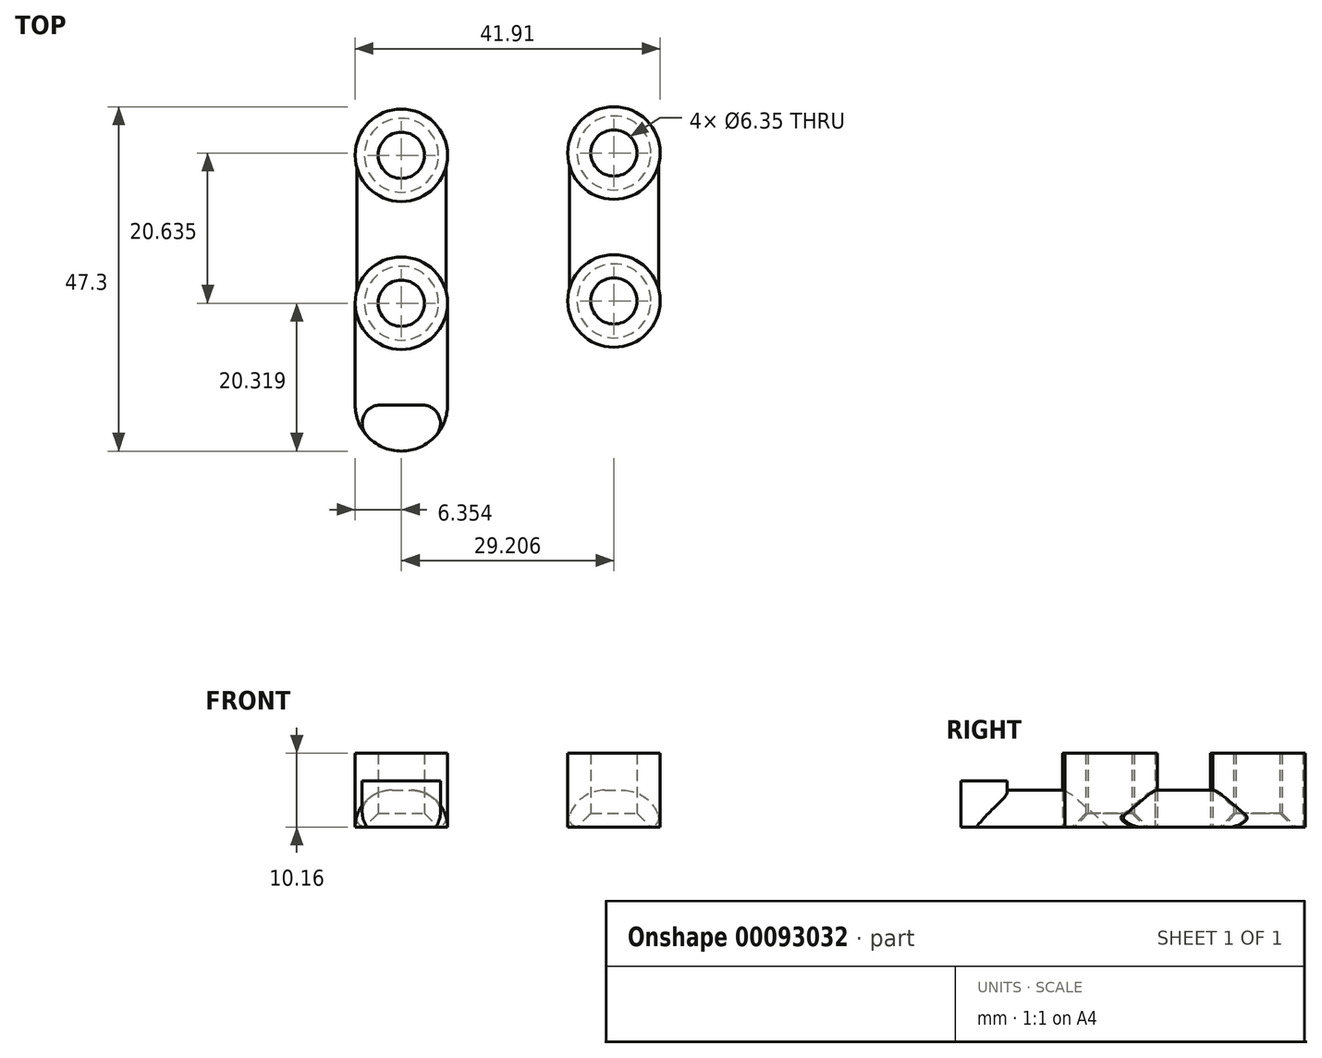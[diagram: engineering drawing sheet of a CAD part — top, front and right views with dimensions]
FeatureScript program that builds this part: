
annotation { "Feature Type Name" : "Feature", "Feature Type Description" : "" }
export const myFeature = defineFeature(function(context is Context, id is Id, definition is map)
    precondition{}
    {
        {
            var Q0;
            Q0=qCreatedBy(makeId("Top.planeOp"),FACE);
            var sketch = newSketch(context, id + "F0", { "sketchPlane" : qUnion([Q0])});
            skCircle(sketch, "E0", {"center": v(-29.2, 13.35) * mm, "radius": 6.35 * mm});
            skCircle(sketch, "E1", {"center": v(-29.2, 13.35) * mm, "radius": 3.18 * mm});
            skLineSegment(sketch, "E2", {"start": v(-22.86, 13.35) * mm, "end": v(-22.86, -20.94) * mm});
            skLineSegment(sketch, "E3", {"start": v(-35.56, 13.35) * mm, "end": v(-35.56, -20.94) * mm});
            skCircle(sketch, "E4", {"center": v(-29.2, -6.97) * mm, "radius": 3.18 * mm});
            skCircle(sketch, "E5", {"center": v(-29.2, -6.97) * mm, "radius": 6.35 * mm});
            skLineSegment(sketch, "E6", {"start": v(-29.23, -27.3) * mm, "end": v(-29.23, -27.3) * mm});
            skPoint(sketch, "E7.visualSharp", {"position": v(-35.56, -27.27) * mm});
            skArc(sketch, "E7.filletArc", {"start": v(-35.56, -20.94) * mm, "mid": v(-33.7, -25.42) * mm, "end": v(-29.23, -27.3) * mm});
            skPoint(sketch, "E8.visualSharp", {"position": v(-22.86, -27.32) * mm});
            skArc(sketch, "E8.filletArc", {"start": v(-29.23, -27.3) * mm, "mid": v(-24.72, -25.44) * mm, "end": v(-22.86, -20.94) * mm});
            skLineSegment(sketch, "E9", {"start": v(-35.56, -20.94) * mm, "end": v(-22.86, -20.94) * mm});
            skPoint(sketch, "E10", {"position": v(-29.2, -13.32) * mm});
            skLineSegment(sketch, "E11", {"start": v(-35.56, -13.32) * mm, "end": v(-22.86, -13.32) * mm});
            skSolve(sketch);
        }
        {
            var Q0;
            Q0=makeQuery(id+"F0.imprint","IMPRINT",FACE,{"disambiguationData":[TD([[makeQuery(id+"F0.imprint","IMPRINT",EDGE,{"derivedFrom":sQuery(id+"F0.wireOp",EDGE,"0VF9o3LT-8eu0-zfYK-Zzd0-NjMuDNmUeefI")}),-1.0]])]});
            var Q1;
            Q1=makeQuery(id+"F0.imprint","IMPRINT",FACE,{"disambiguationData":[TD([[makeQuery(id+"F0.imprint","IMPRINT",EDGE,{"derivedFrom":sQuery(id+"F0.wireOp",EDGE,"E1")}),-1.0]])]});
            var Q2;
            Q2=makeQuery(id+"F0.imprint","IMPRINT",FACE,{"disambiguationData":[TD([[makeQuery(id+"F0.imprint","IMPRINT",EDGE,{"derivedFrom":sQuery(id+"F0.wireOp",EDGE,"E4")}),-1.0]])]});
            var Q3;
            Q3=makeQuery(id+"F0.imprint","IMPRINT",FACE,{"disambiguationData":[TD([[makeQuery(id+"F0.imprint","IMPRINT",EDGE,{"derivedFrom":sQuery(id+"F0.wireOp",EDGE,"E1")}),1.0]])]});
            var Q4;
            Q4=makeQuery(id+"F0.imprint","IMPRINT",FACE,{"disambiguationData":[TD([[makeQuery(id+"F0.imprint","IMPRINT",EDGE,{"derivedFrom":sQuery(id+"F0.wireOp",EDGE,"E4")}),1.0]])]});
            extrude(context, id + "F1", {"entities" : qUnion([Q0, Q1, Q2, Q3, Q4]), "depth" : 10.16 * mm});
        }
        {
            var Q0;
            {var subQ0=sQuery(id+"F0.wireOp",EDGE,"RrL4ANr4-QjHu-QYMl-nBRi-zhhbmreRRQpT");Q0=makeQuery(id+"F0.imprint","IMPRINT",FACE,{"disambiguationData":[TD([[makeQuery(id+"F0.imprint","IMPRINT",EDGE,{"derivedFrom":subQ0}),1.0]])]});}
            var Q1;
            {var subQ4=sQuery(id+"F0.wireOp",EDGE,"E9");Q1=makeQuery(id+"F0.imprint","IMPRINT",FACE,{"disambiguationData":[TD([[makeQuery(id+"F0.imprint","IMPRINT",EDGE,{"derivedFrom":subQ4}),1.0]])]});}
            var Q2;
            {var subQ0=sQuery(id+"F0.wireOp",EDGE,"E2");var subQ1=sQuery(id+"F0.wireOp",EDGE,"E0");var subQ2=makeQuery(id+"F0.imprint","INTERSECT",VERTEX,{"derivedFrom":[subQ1,subQ0]});Q2=makeQuery(id+"F0.imprint","IMPRINT",FACE,{"disambiguationData":[TD([[makeQuery(id+"F0.imprint","IMPRINT",EDGE,{"disambiguationData":[TD([[subQ2,1.0]])],"derivedFrom":subQ1}),-1.0]])]});}
            var Q3;
            {var subQ0=sQuery(id+"F0.wireOp",EDGE,"E11");var subQ1=sQuery(id+"F0.wireOp",EDGE,"E3");var subQ2=makeQuery(id+"F0.imprint","INTERSECT",VERTEX,{"derivedFrom":[subQ1,subQ0]});Q3=makeQuery(id+"F0.imprint","IMPRINT",FACE,{"disambiguationData":[TD([[makeQuery(id+"F0.imprint","IMPRINT",EDGE,{"disambiguationData":[TD([[subQ2,1.0]])],"derivedFrom":subQ1}),1.0]])]});}
            var Q4;
            {var subQ0=sQuery(id+"F0.wireOp",EDGE,"E11");var subQ1=sQuery(id+"F0.wireOp",EDGE,"E2");var subQ2=makeQuery(id+"F0.imprint","INTERSECT",VERTEX,{"derivedFrom":[subQ1,subQ0]});Q4=makeQuery(id+"F0.imprint","IMPRINT",FACE,{"disambiguationData":[TD([[makeQuery(id+"F0.imprint","IMPRINT",EDGE,{"disambiguationData":[TD([[subQ2,1.0]])],"derivedFrom":subQ1}),-1.0]])]});}
            extrude(context, id + "F2", {"entities" : qUnion([Q0, Q1, Q2, Q3, Q4]), "depth" : 5.08 * mm});
        }
        {
            var Q0;
            Q0=makeQuery(id+"F0.imprint","IMPRINT",FACE,{"disambiguationData":[TD([[makeQuery(id+"F0.imprint","IMPRINT",EDGE,{"derivedFrom":sQuery(id+"F0.wireOp",EDGE,"E7.filletArc")}),1.0]])]});
            extrude(context, id + "F3", {"entities" : qUnion([Q0]), "operationType" : NewBodyOperationType.ADD, "depth" : 6.35 * mm});
        }
        {
            var Q0;
            {var subQ0=sQuery(id+"F0.wireOp",EDGE,"RrL4ANr4-QjHu-QYMl-nBRi-zhhbmreRRQpT");var subQ1=sQuery(id+"F0.wireOp",EDGE,"8041460e-15c7-452b-9ff8-86583f3ae971.filletArc");var subQ2=sQuery(id+"F0.wireOp",EDGE,"OiBgF3Y6-Kc90-e7Jp-mXld-NBTCDyDgULQI.left");var subQ3=makeQuery(id+"F3.opExtrude","SWEPT_EDGE",EDGE,{"disambiguationData":[OSD([subQ2,subQ1,subQ0])]});Q0=makeQuery(id+"F5.opFillet","MERGE",EDGE,{"derivedFrom":[makeQuery(id+"F3.boolean.opBoolean","MERGE",EDGE,{"derivedFrom":[makeQuery(id+"F2.opExtrude","SWEPT_EDGE",EDGE,{"disambiguationData":[OSD([subQ2,subQ1,subQ0])]}),subQ3]}),makeQuery(id+"F3.boolean.opBoolean","SPLIT",EDGE,{"derivedFrom":subQ3})]});}
            var Q1;
            Q1=makeQuery(id+"F1.opExtrude","SWEPT_EDGE",EDGE,{"disambiguationData":[OSD([sQuery(id+"F0.wireOp",EDGE,"OiBgF3Y6-Kc90-e7Jp-mXld-NBTCDyDgULQI.left"),sQuery(id+"F0.wireOp",EDGE,"n4Bth454-DqkM-WBTY-o2g9-bsl29lXR5TTy")])]});
            var Q2;
            {var subQ0=sQuery(id+"F0.wireOp",EDGE,"RrL4ANr4-QjHu-QYMl-nBRi-zhhbmreRRQpT");var subQ1=sQuery(id+"F0.wireOp",EDGE,"7f0ffca3-70b9-4b19-ad79-aae9e87e8456.filletArc");var subQ2=sQuery(id+"F0.wireOp",EDGE,"OiBgF3Y6-Kc90-e7Jp-mXld-NBTCDyDgULQI.right");var subQ3=makeQuery(id+"F3.opExtrude","SWEPT_EDGE",EDGE,{"disambiguationData":[OSD([subQ2,subQ1,subQ0])]});Q2=makeQuery(id+"F5.opFillet","MERGE",EDGE,{"derivedFrom":[makeQuery(id+"F3.boolean.opBoolean","MERGE",EDGE,{"derivedFrom":[makeQuery(id+"F2.opExtrude","SWEPT_EDGE",EDGE,{"disambiguationData":[OSD([subQ2,subQ1,subQ0])]}),subQ3]}),makeQuery(id+"F3.boolean.opBoolean","SPLIT",EDGE,{"derivedFrom":subQ3})]});}
            var Q3;
            Q3=makeQuery(id+"F1.opExtrude","SWEPT_EDGE",EDGE,{"disambiguationData":[OSD([sQuery(id+"F0.wireOp",EDGE,"OiBgF3Y6-Kc90-e7Jp-mXld-NBTCDyDgULQI.right"),sQuery(id+"F0.wireOp",EDGE,"n4Bth454-DqkM-WBTY-o2g9-bsl29lXR5TTy")])]});
            var Q4;
            Q4=makeQuery(id+"F3.boolean.opBoolean","SPLIT",EDGE,{"derivedFrom":makeQuery(id+"F3.opExtrude","SWEPT_EDGE",EDGE,{"disambiguationData":[OSD([sQuery(id+"F0.wireOp",EDGE,"E3"),sQuery(id+"F0.wireOp",EDGE,"E7.filletArc"),sQuery(id+"F0.wireOp",EDGE,"E9")])]})});
            var Q5;
            Q5=makeQuery(id+"F3.boolean.opBoolean","SPLIT",EDGE,{"derivedFrom":makeQuery(id+"F3.opExtrude","SWEPT_EDGE",EDGE,{"disambiguationData":[OSD([sQuery(id+"F0.wireOp",EDGE,"E2"),sQuery(id+"F0.wireOp",EDGE,"E8.filletArc"),sQuery(id+"F0.wireOp",EDGE,"E9")])]})});
            fillet(context, id + "F4", {"entities" : qUnion([Q0, Q1, Q2, Q3, Q4, Q5]), "radius" : 2.54 * mm, "tangentPropagation" : true, "allowEdgeOverflow" : false});
        }
        {
            var Q0;
            {var subQ0=sQuery(id+"F0.wireOp",EDGE,"E3");Q0=makeQuery(id+"F2.opExtrude","CAP_EDGE",EDGE,{"disambiguationData":[OSD([subQ0]),TDD([makeQuery(id+"F0.imprint","IMPRINT",EDGE,{"disambiguationData":[TD([[makeQuery(id+"F0.imprint","INTERSECT",VERTEX,{"derivedFrom":[sQuery(id+"F0.wireOp",EDGE,"E0"),subQ0]}),-1.0]])],"derivedFrom":subQ0})])],"isStart":false});}
            var Q1;
            {var subQ0=sQuery(id+"F0.wireOp",EDGE,"E2");Q1=makeQuery(id+"F2.opExtrude","CAP_EDGE",EDGE,{"disambiguationData":[OSD([subQ0]),TDD([makeQuery(id+"F0.imprint","IMPRINT",EDGE,{"disambiguationData":[TD([[makeQuery(id+"F0.imprint","INTERSECT",VERTEX,{"derivedFrom":[sQuery(id+"F0.wireOp",EDGE,"E0"),subQ0]}),-1.0]])],"derivedFrom":subQ0})])],"isStart":false});}
            var Q2;
            {var subQ0=sQuery(id+"F0.wireOp",EDGE,"E2");var subQ1=makeQuery(id+"F0.imprint","INTERSECT",VERTEX,{"derivedFrom":[subQ0,sQuery(id+"F0.wireOp",EDGE,"E11")]});Q2=makeQuery(id+"F2.opExtrude","CAP_EDGE",EDGE,{"disambiguationData":[OSD([subQ0]),TDD([makeQuery(id+"F0.imprint","IMPRINT",EDGE,{"disambiguationData":[TD([[subQ1,1.0]])],"derivedFrom":subQ0}),makeQuery(id+"F0.imprint","IMPRINT",EDGE,{"disambiguationData":[TD([[subQ1,-1.0]])],"derivedFrom":subQ0})])],"isStart":false});}
            var Q3;
            {var subQ0=sQuery(id+"F0.wireOp",EDGE,"E3");var subQ1=makeQuery(id+"F0.imprint","INTERSECT",VERTEX,{"derivedFrom":[subQ0,sQuery(id+"F0.wireOp",EDGE,"E11")]});Q3=makeQuery(id+"F2.opExtrude","CAP_EDGE",EDGE,{"disambiguationData":[OSD([subQ0]),TDD([makeQuery(id+"F0.imprint","IMPRINT",EDGE,{"disambiguationData":[TD([[subQ1,1.0]])],"derivedFrom":subQ0}),makeQuery(id+"F0.imprint","IMPRINT",EDGE,{"disambiguationData":[TD([[subQ1,-1.0]])],"derivedFrom":subQ0})])],"isStart":false});}
            fillet(context, id + "F5", {"entities" : qUnion([Q0, Q1, Q2, Q3]), "radius" : 5.08 * mm, "tangentPropagation" : true, "allowEdgeOverflow" : false});
        }
        {
            var Q0;
            Q0=sQuery(id+"F0.wireOp",VERTEX,"E0.center");
            var Q1;
            Q1=sQuery(id+"F0.wireOp",VERTEX,"E4.center");
            var Q2;
            Q2=makeQuery(id+"F1.opExtrude","SWEPT_BODY",BODY,{"disambiguationData":[OSD([sQuery(id+"F0.wireOp",EDGE,"E0")])]});
            var Q3;
            Q3=makeQuery(id+"F1.opExtrude","SWEPT_BODY",BODY,{"disambiguationData":[OSD([sQuery(id+"F0.wireOp",EDGE,"E5")])]});
            hole(context, id + "F6", {"style" : HoleStyle.C_SINK, "endStyle" : HoleEndStyle.THROUGH, "oppositeDirection" : true, "holeDiameter" : 6.35 * mm, "cSinkDiameter" : 10.16 * mm, "cSinkAngle" : 90 * degree, "locations" : qUnion([Q0, Q1]), "scope" : qUnion([Q2, Q3]), "isTappedThrough" : true});
        }
        {
            var Q0;
            Q0=qCreatedBy(makeId("Top.planeOp"),FACE);
            var sketch = newSketch(context, id + "F7", { "sketchPlane" : qUnion([Q0])});
            skCircle(sketch, "E12", {"center": v(0, 13.66) * mm, "radius": 3.18 * mm});
            skCircle(sketch, "E13", {"center": v(0, 13.66) * mm, "radius": 6.35 * mm});
            skCircle(sketch, "E14", {"center": v(0, -6.66) * mm, "radius": 3.18 * mm});
            skCircle(sketch, "E15", {"center": v(0, -6.66) * mm, "radius": 6.35 * mm});
            skLineSegment(sketch, "E16", {"start": v(-6.35, 13.66) * mm, "end": v(-6.35, -6.66) * mm});
            skLineSegment(sketch, "E17", {"start": v(6.35, 13.66) * mm, "end": v(6.35, -6.66) * mm});
            skPoint(sketch, "E18", {"position": v(0, 7.31) * mm});
            skPoint(sketch, "E19", {"position": v(0, -0.3) * mm});
            skSolve(sketch);
        }
        {
            var Q0;
            Q0=makeQuery(id+"F7.imprint","IMPRINT",FACE,{"disambiguationData":[TD([[makeQuery(id+"F7.imprint","IMPRINT",EDGE,{"derivedFrom":sQuery(id+"F7.wireOp",EDGE,"E12")}),-1.0]])]});
            var Q1;
            Q1=makeQuery(id+"F7.imprint","IMPRINT",FACE,{"disambiguationData":[TD([[makeQuery(id+"F7.imprint","IMPRINT",EDGE,{"derivedFrom":sQuery(id+"F7.wireOp",EDGE,"E14")}),-1.0]])]});
            var Q2;
            Q2=makeQuery(id+"F7.imprint","IMPRINT",FACE,{"disambiguationData":[TD([[makeQuery(id+"F7.imprint","IMPRINT",EDGE,{"derivedFrom":sQuery(id+"F7.wireOp",EDGE,"E14")}),1.0]])]});
            var Q3;
            Q3=makeQuery(id+"F7.imprint","IMPRINT",FACE,{"disambiguationData":[TD([[makeQuery(id+"F7.imprint","IMPRINT",EDGE,{"derivedFrom":sQuery(id+"F7.wireOp",EDGE,"E12")}),1.0]])]});
            extrude(context, id + "F8", {"entities" : qUnion([Q0, Q1, Q2, Q3]), "depth" : 10.16 * mm});
        }
        {
            var Q0;
            {var subQ0=sQuery(id+"F7.wireOp",EDGE,"E16");Q0=makeQuery(id+"F7.imprint","IMPRINT",FACE,{"disambiguationData":[TD([[makeQuery(id+"F7.imprint","IMPRINT",EDGE,{"derivedFrom":subQ0}),1.0]])]});}
            extrude(context, id + "F9", {"entities" : qUnion([Q0]), "depth" : 5.08 * mm});
        }
        {
            var Q0;
            Q0=makeQuery(id+"F9.opExtrude","CAP_EDGE",EDGE,{"disambiguationData":[OSD([sQuery(id+"F7.wireOp",EDGE,"E16")])],"isStart":false});
            var Q1;
            Q1=makeQuery(id+"F9.opExtrude","CAP_EDGE",EDGE,{"disambiguationData":[OSD([sQuery(id+"F7.wireOp",EDGE,"E17")])],"isStart":false});
            fillet(context, id + "F10", {"entities" : qUnion([Q0, Q1]), "radius" : 5.08 * mm, "tangentPropagation" : true, "allowEdgeOverflow" : false});
        }
        {
            var Q0;
            Q0=sQuery(id+"F7.wireOp",VERTEX,"E14.center");
            var Q1;
            Q1=sQuery(id+"F7.wireOp",VERTEX,"E12.center");
            var Q2;
            Q2=makeQuery(id+"F8.opExtrude","SWEPT_BODY",BODY,{"disambiguationData":[OSD([sQuery(id+"F7.wireOp",EDGE,"E15")])]});
            var Q3;
            Q3=makeQuery(id+"F8.opExtrude","SWEPT_BODY",BODY,{"disambiguationData":[OSD([sQuery(id+"F7.wireOp",EDGE,"E13")])]});
            hole(context, id + "F11", {"style" : HoleStyle.C_SINK, "endStyle" : HoleEndStyle.THROUGH, "oppositeDirection" : true, "holeDiameter" : 6.35 * mm, "cSinkDiameter" : 10.16 * mm, "cSinkAngle" : 90 * degree, "locations" : qUnion([Q0, Q1]), "scope" : qUnion([Q2, Q3]), "isTappedThrough" : true});
        }
        {
            var Q0;
            {var subQ0=sQuery(id+"F7.wireOp",EDGE,"E17");Q0=makeQuery(id+"F10.opFillet","BLEND_EDGE",EDGE,{"blendedFrom":[makeQuery(id+"F9.opExtrude","CAP_EDGE",EDGE,{"disambiguationData":[OSD([subQ0])],"isStart":false}),makeQuery(id+"F9.opExtrude","CAP_FACE",FACE,{"disambiguationData":[OSD([sQuery(id+"F7.wireOp",EDGE,"E13"),sQuery(id+"F7.wireOp",EDGE,"E15"),sQuery(id+"F7.wireOp",EDGE,"E16"),subQ0])],"isStart":true})],"blendedInto":[makeQuery(id+"F9.opExtrude","CAP_FACE",FACE,{"disambiguationData":[OSD([sQuery(id+"F7.wireOp",EDGE,"E13"),sQuery(id+"F7.wireOp",EDGE,"E15"),sQuery(id+"F7.wireOp",EDGE,"E16"),subQ0])],"isStart":true})]});}
            var Q1;
            {var subQ0=sQuery(id+"F7.wireOp",EDGE,"E16");Q1=makeQuery(id+"F10.opFillet","BLEND_EDGE",EDGE,{"blendedFrom":[makeQuery(id+"F9.opExtrude","CAP_EDGE",EDGE,{"disambiguationData":[OSD([subQ0])],"isStart":false}),makeQuery(id+"F9.opExtrude","CAP_FACE",FACE,{"disambiguationData":[OSD([sQuery(id+"F7.wireOp",EDGE,"E13"),sQuery(id+"F7.wireOp",EDGE,"E15"),subQ0,sQuery(id+"F7.wireOp",EDGE,"E17")])],"isStart":true})],"blendedInto":[makeQuery(id+"F9.opExtrude","CAP_FACE",FACE,{"disambiguationData":[OSD([sQuery(id+"F7.wireOp",EDGE,"E13"),sQuery(id+"F7.wireOp",EDGE,"E15"),subQ0,sQuery(id+"F7.wireOp",EDGE,"E17")])],"isStart":true})]});}
            var Q2;
            {var subQ0=sQuery(id+"F0.wireOp",EDGE,"E5");var subQ1=sQuery(id+"F0.wireOp",EDGE,"E2");var subQ2=sQuery(id+"F0.wireOp",EDGE,"E0");Q2=makeQuery(id+"F5.opFillet","BLEND_EDGE",EDGE,{"blendedFrom":[makeQuery(id+"F2.opExtrude","CAP_EDGE",EDGE,{"disambiguationData":[OSD([subQ1]),TDD([makeQuery(id+"F0.imprint","IMPRINT",EDGE,{"disambiguationData":[TD([[makeQuery(id+"F0.imprint","INTERSECT",VERTEX,{"derivedFrom":[subQ2,subQ1]}),-1.0]])],"derivedFrom":subQ1})])],"isStart":false}),makeQuery(id+"F2.opExtrude","CAP_FACE",FACE,{"disambiguationData":[OSD([subQ2,subQ1,sQuery(id+"F0.wireOp",EDGE,"E3"),subQ0])],"isStart":true})],"blendedInto":[makeQuery(id+"F2.opExtrude","CAP_FACE",FACE,{"disambiguationData":[OSD([subQ2,subQ1,sQuery(id+"F0.wireOp",EDGE,"E3"),subQ0])],"isStart":true})]});}
            var Q3;
            {var subQ0=sQuery(id+"F0.wireOp",EDGE,"E5");var subQ1=sQuery(id+"F0.wireOp",EDGE,"E3");var subQ2=sQuery(id+"F0.wireOp",EDGE,"E0");Q3=makeQuery(id+"F5.opFillet","BLEND_EDGE",EDGE,{"blendedFrom":[makeQuery(id+"F2.opExtrude","CAP_EDGE",EDGE,{"disambiguationData":[OSD([subQ1]),TDD([makeQuery(id+"F0.imprint","IMPRINT",EDGE,{"disambiguationData":[TD([[makeQuery(id+"F0.imprint","INTERSECT",VERTEX,{"derivedFrom":[subQ2,subQ1]}),-1.0]])],"derivedFrom":subQ1})])],"isStart":false}),makeQuery(id+"F2.opExtrude","CAP_FACE",FACE,{"disambiguationData":[OSD([subQ2,sQuery(id+"F0.wireOp",EDGE,"E2"),subQ1,subQ0])],"isStart":true})],"blendedInto":[makeQuery(id+"F2.opExtrude","CAP_FACE",FACE,{"disambiguationData":[OSD([subQ2,sQuery(id+"F0.wireOp",EDGE,"E2"),subQ1,subQ0])],"isStart":true})]});}
            var Q4;
            {var subQ0=sQuery(id+"F0.wireOp",EDGE,"E9");var subQ1=sQuery(id+"F0.wireOp",EDGE,"E8.filletArc");var subQ2=sQuery(id+"F0.wireOp",EDGE,"E5");var subQ3=sQuery(id+"F0.wireOp",EDGE,"E2");var subQ4=makeQuery(id+"F0.imprint","INTERSECT",VERTEX,{"derivedFrom":[subQ3,sQuery(id+"F0.wireOp",EDGE,"E11")]});Q4=makeQuery(id+"F5.opFillet","BLEND_EDGE",EDGE,{"blendedFrom":[makeQuery(id+"F2.opExtrude","CAP_EDGE",EDGE,{"disambiguationData":[OSD([subQ3]),TDD([makeQuery(id+"F0.imprint","IMPRINT",EDGE,{"disambiguationData":[TD([[subQ4,1.0]])],"derivedFrom":subQ3}),makeQuery(id+"F0.imprint","IMPRINT",EDGE,{"disambiguationData":[TD([[subQ4,-1.0]])],"derivedFrom":subQ3})])],"isStart":false}),makeQuery(id+"F3.boolean.opBoolean","MERGE",FACE,{"derivedFrom":[makeQuery(id+"F2.opExtrude","CAP_FACE",FACE,{"disambiguationData":[OSD([subQ3,sQuery(id+"F0.wireOp",EDGE,"E3"),subQ2,subQ0])],"isStart":true}),makeQuery(id+"F3.opExtrude","CAP_FACE",FACE,{"disambiguationData":[OSD([sQuery(id+"F0.wireOp",EDGE,"E7.filletArc"),subQ1,subQ0])],"isStart":true})]})],"blendedInto":[makeQuery(id+"F3.boolean.opBoolean","MERGE",FACE,{"derivedFrom":[makeQuery(id+"F2.opExtrude","CAP_FACE",FACE,{"disambiguationData":[OSD([subQ3,sQuery(id+"F0.wireOp",EDGE,"E3"),subQ2,subQ0])],"isStart":true}),makeQuery(id+"F3.opExtrude","CAP_FACE",FACE,{"disambiguationData":[OSD([sQuery(id+"F0.wireOp",EDGE,"E7.filletArc"),subQ1,subQ0])],"isStart":true})]})]});}
            var Q5;
            {var subQ0=sQuery(id+"F0.wireOp",EDGE,"E9");var subQ1=sQuery(id+"F0.wireOp",EDGE,"E7.filletArc");var subQ2=sQuery(id+"F0.wireOp",EDGE,"E5");var subQ3=sQuery(id+"F0.wireOp",EDGE,"E3");var subQ4=makeQuery(id+"F0.imprint","INTERSECT",VERTEX,{"derivedFrom":[subQ3,sQuery(id+"F0.wireOp",EDGE,"E11")]});Q5=makeQuery(id+"F5.opFillet","BLEND_EDGE",EDGE,{"blendedFrom":[makeQuery(id+"F2.opExtrude","CAP_EDGE",EDGE,{"disambiguationData":[OSD([subQ3]),TDD([makeQuery(id+"F0.imprint","IMPRINT",EDGE,{"disambiguationData":[TD([[subQ4,1.0]])],"derivedFrom":subQ3}),makeQuery(id+"F0.imprint","IMPRINT",EDGE,{"disambiguationData":[TD([[subQ4,-1.0]])],"derivedFrom":subQ3})])],"isStart":false}),makeQuery(id+"F3.boolean.opBoolean","MERGE",FACE,{"derivedFrom":[makeQuery(id+"F2.opExtrude","CAP_FACE",FACE,{"disambiguationData":[OSD([sQuery(id+"F0.wireOp",EDGE,"E2"),subQ3,subQ2,subQ0])],"isStart":true}),makeQuery(id+"F3.opExtrude","CAP_FACE",FACE,{"disambiguationData":[OSD([subQ1,sQuery(id+"F0.wireOp",EDGE,"E8.filletArc"),subQ0])],"isStart":true})]})],"blendedInto":[makeQuery(id+"F3.boolean.opBoolean","MERGE",FACE,{"derivedFrom":[makeQuery(id+"F2.opExtrude","CAP_FACE",FACE,{"disambiguationData":[OSD([sQuery(id+"F0.wireOp",EDGE,"E2"),subQ3,subQ2,subQ0])],"isStart":true}),makeQuery(id+"F3.opExtrude","CAP_FACE",FACE,{"disambiguationData":[OSD([subQ1,sQuery(id+"F0.wireOp",EDGE,"E8.filletArc"),subQ0])],"isStart":true})]})]});}
            fillet(context, id + "F12", {"entities" : qUnion([Q0, Q1, Q2, Q3, Q4, Q5]), "radius" : 1.27 * mm, "tangentPropagation" : true, "allowEdgeOverflow" : false});
        }
    });
